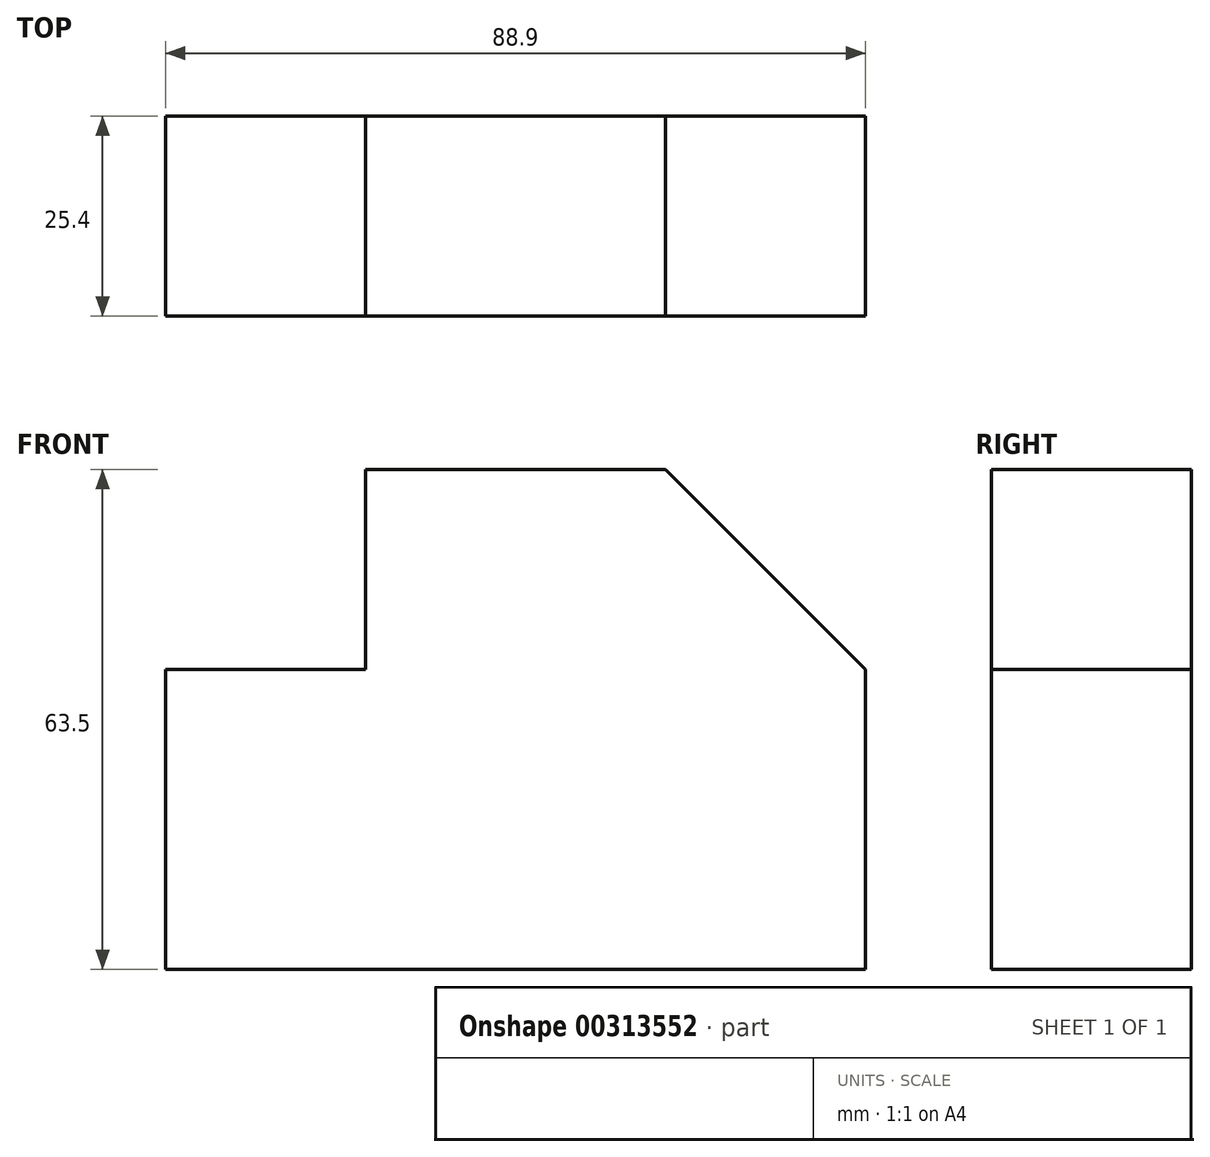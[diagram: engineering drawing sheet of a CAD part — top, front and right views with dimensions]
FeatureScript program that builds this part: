
annotation { "Feature Type Name" : "Feature", "Feature Type Description" : "" }
export const myFeature = defineFeature(function(context is Context, id is Id, definition is map)
    precondition{}
    {
        {
            var Q0;
            Q0=qCreatedBy(makeId("Front.planeOp"),FACE);
            var sketch = newSketch(context, id + "F0", { "sketchPlane" : qUnion([Q0])});
            skLineSegment(sketch, "E0", {"start": v(47.89, -41.9) * mm, "end": v(-41.01, -41.9) * mm});
            skLineSegment(sketch, "E1", {"start": v(-41.01, -41.9) * mm, "end": v(-41.01, -3.8) * mm});
            skLineSegment(sketch, "E2", {"start": v(-41.01, -3.8) * mm, "end": v(-15.61, -3.8) * mm});
            skLineSegment(sketch, "E3", {"start": v(47.89, -41.9) * mm, "end": v(47.89, -3.8) * mm});
            skLineSegment(sketch, "E4", {"start": v(-15.61, -3.8) * mm, "end": v(-15.61, 21.6) * mm});
            skLineSegment(sketch, "E5", {"start": v(-15.61, 21.6) * mm, "end": v(22.49, 21.6) * mm});
            skLineSegment(sketch, "E6", {"start": v(22.49, 21.6) * mm, "end": v(47.89, -3.8) * mm});
            skSolve(sketch);
        }
        {
            var Q0;
            Q0=makeQuery(id+"F0.imprint","IMPRINT",FACE,{"disambiguationData":[TD([[makeQuery(id+"F0.imprint","IMPRINT",EDGE,{"derivedFrom":sQuery(id+"F0.wireOp",EDGE,"E0")}),-1.0]])]});
            extrude(context, id + "F1", {"entities" : qUnion([Q0]), "depth" : 25.4 * mm});
        }
    });
